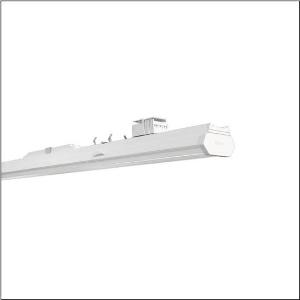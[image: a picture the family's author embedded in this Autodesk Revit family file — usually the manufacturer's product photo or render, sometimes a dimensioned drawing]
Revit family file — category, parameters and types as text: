
# Revit family: licross_r__21_protected_mo_52td117n485g_f66a
name_source: partatom
category: Lighting Fixtures
units: mm (PartAtom-declared; Revit-internal decimal feet)

## family parameters
Cut with Voids When Loaded = No
Host = Face
Light Source = No
Part Type = Normal
Room Calculation Point = No
Round Connector Dimension = Use Diameter
Shared = No

## types (1)
- Licross® 21 Protected MO (1 x LED, 8570 lm, 47.9 W, 4000K)
    Apparent Load = 48 VA
    CIE Flux Codes = 83 94 98 100 100
    Color Rendering = 80
    Color Temperature = 4000K
    Default Elevation = 1800 mm
    Description = Licross® 21 Protected MO, luminaire insert, of sheet steel, galvanised, coil coated, white, length: 1.500mm, width: 66mm, height: 67mm, LED rated luminous flux: 8.570lm, light colour: 840, control gear: ON/OFF, with plug, 3-pole, with phase selection, mains connection: 220..240V, AC, 50/60Hz, rated input power: 48W, halogen-free wiring, primary light control with lens, of plastic, primary optical cover: cover, of PMMA, light emission: direct distribution, primary light characteristic: symmetric, protection rating (complete): IP54, insulation class (complete): insulation class I (protective earthing), certification: CE, ENEC, VDE, UKCA, protection symbol: D if used in an environment with non-conductive dust loads with corresponding accessories, impact resistance: IK06, permissible ambient temperature for indoor applications: -35..+45°C, corresponds to IFS (International Featured Standards) requirements for safety and quality in the food industry, reducing of maximum allowable ambient temperature of 5°C with ceiling mounting, LABS conformity tested according to VDMA 24364:2018-05, packaging unit: 1 piece
    Height = 92 mm
    Lamp = 1 x LED
    Lamp Light Flux = 8570 lm
    Lamp Power = 47.9 W
    Lamp count = 1
    Length = 1500 mm
    Luminous efficacy = 179 lm/W
    Manufacturer = Siteco
    ModVariant = No
    Model = 52TD117N485G
    Mounting Place = Ceiling
    Mounting Type = Pendant
    Number of Poles = 1
    OnlyDefault = Yes
    Power Factor = 1
    Product Name = Licross® 21 Protected MO
    Product group = luminaire insert
    ProductGroupID = 901
    Protection Class = Protection class I
    Protection Degree = IP 54
    RLX_Detail_Level = 1
    RLX_Emergency_Light_Flux = 0 lm
    RLX_Emergency_Type = 0
    RLX_Emergency_Type_DB = No
    RlxData = <blob elided: 20457 chars, md5=af18bcd5>
    Socket = socket
    Standby Power = 0 W
    System Light Flux = 8570 lm
    System Power = 48 W
    Type Comments = Product without accessories
    Type Image = l_1256148.jpg
    URL = http://relux.com
    VarID = ---
    Voltage = 0 V
    Weight = 0.00 kg
    Width = 88 mm

## geometry (parser evidence)
native form markers: Blend x4, Sweep x12
no freeform markers — native parametric forms only
